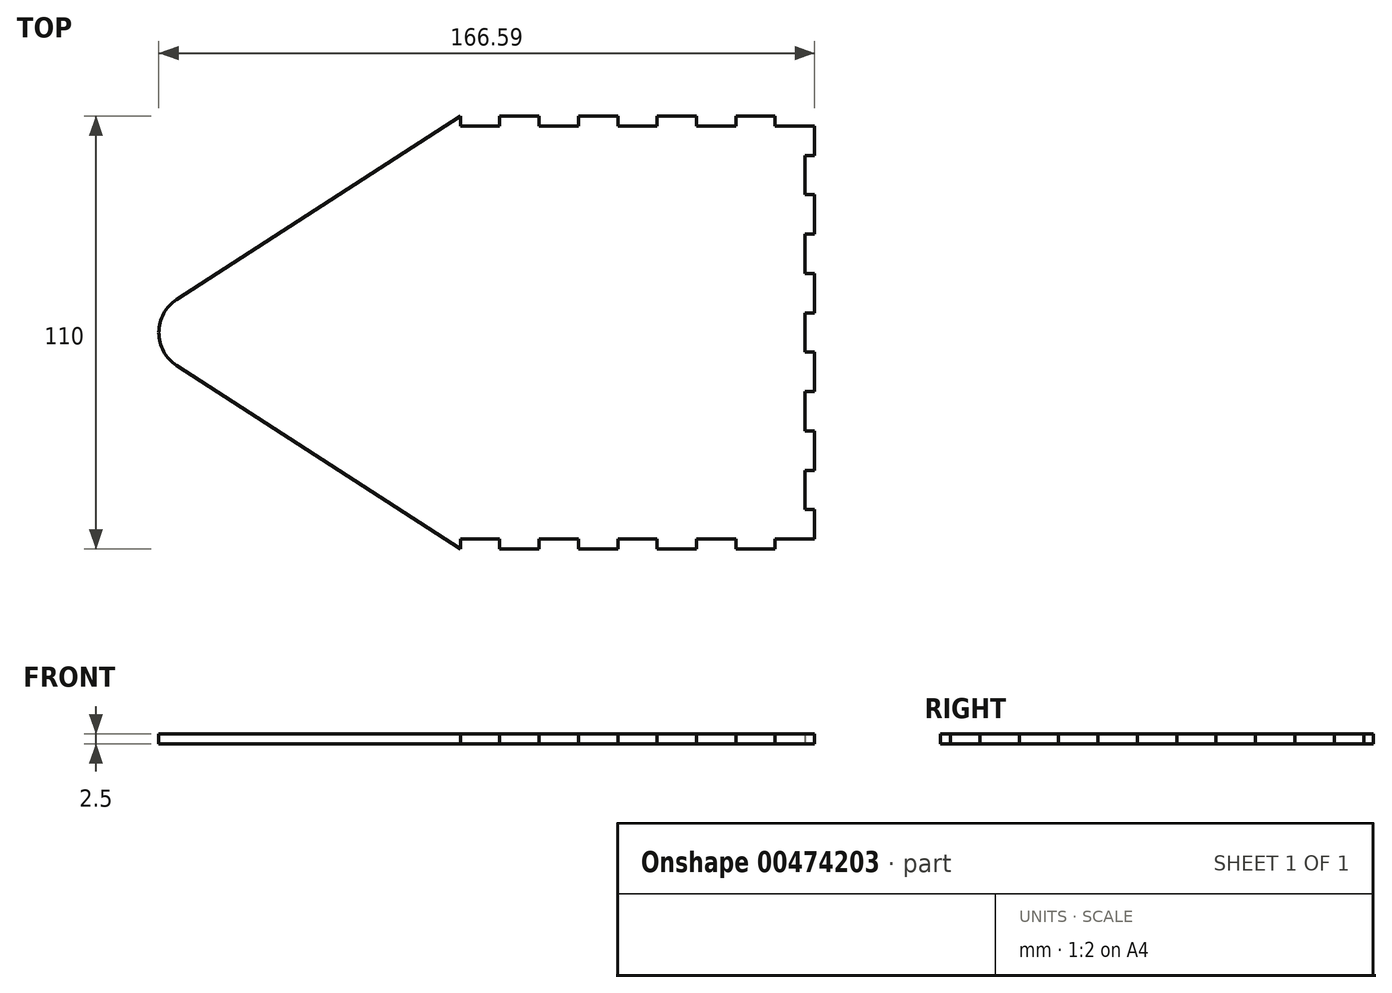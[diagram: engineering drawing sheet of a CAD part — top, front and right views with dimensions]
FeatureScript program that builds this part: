
annotation { "Feature Type Name" : "Feature", "Feature Type Description" : "" }
export const myFeature = defineFeature(function(context is Context, id is Id, definition is map)
    precondition{}
    {
        {
            var Q0;
            Q0=qCreatedBy(makeId("Top.planeOp"),FACE);
            var sketch = newSketch(context, id + "F0", { "sketchPlane" : qUnion([Q0])});
            skLineSegment(sketch, "E0.bottom", {"start": v(75, -55) * mm, "end": v(-15, -55) * mm});
            skLineSegment(sketch, "E0.top", {"start": v(75, 55) * mm, "end": v(-15, 55) * mm});
            skLineSegment(sketch, "E0.left", {"start": v(75, -55) * mm, "end": v(75, 55) * mm});
            skLineSegment(sketch, "E1.bottom", {"start": v(75, 55) * mm, "end": v(65, 55) * mm});
            skLineSegment(sketch, "E1.top", {"start": v(75, 52.5) * mm, "end": v(65, 52.5) * mm});
            skLineSegment(sketch, "E1.left", {"start": v(75, 55) * mm, "end": v(75, 52.5) * mm});
            skLineSegment(sketch, "E1.right", {"start": v(65, 55) * mm, "end": v(65, 52.5) * mm});
            skLineSegment(sketch, "E2.0.1.0", {"start": v(65, -52.5) * mm, "end": v(65, -55) * mm});
            skLineSegment(sketch, "E2.0.1.1", {"start": v(75, -52.5) * mm, "end": v(75, -55) * mm});
            skLineSegment(sketch, "E2.0.1.2", {"start": v(75, -55) * mm, "end": v(65, -55) * mm});
            skLineSegment(sketch, "E2.0.1.3", {"start": v(75, -52.5) * mm, "end": v(65, -52.5) * mm});
            skLineSegment(sketch, "E2.1.0.0", {"start": v(45, 55) * mm, "end": v(45, 52.5) * mm});
            skLineSegment(sketch, "E2.1.0.1", {"start": v(55, 55) * mm, "end": v(55, 52.5) * mm});
            skLineSegment(sketch, "E2.1.0.2", {"start": v(55, 52.5) * mm, "end": v(45, 52.5) * mm});
            skLineSegment(sketch, "E2.1.0.3", {"start": v(55, 55) * mm, "end": v(45, 55) * mm});
            skLineSegment(sketch, "E2.1.1.0", {"start": v(45, -52.5) * mm, "end": v(45, -55) * mm});
            skLineSegment(sketch, "E2.1.1.1", {"start": v(55, -52.5) * mm, "end": v(55, -55) * mm});
            skLineSegment(sketch, "E2.1.1.2", {"start": v(55, -55) * mm, "end": v(45, -55) * mm});
            skLineSegment(sketch, "E2.1.1.3", {"start": v(55, -52.5) * mm, "end": v(45, -52.5) * mm});
            skLineSegment(sketch, "E2.2.0.0", {"start": v(25, 55) * mm, "end": v(25, 52.5) * mm});
            skLineSegment(sketch, "E2.2.0.1", {"start": v(35, 55) * mm, "end": v(35, 52.5) * mm});
            skLineSegment(sketch, "E2.2.0.2", {"start": v(35, 52.5) * mm, "end": v(25, 52.5) * mm});
            skLineSegment(sketch, "E2.2.0.3", {"start": v(35, 55) * mm, "end": v(25, 55) * mm});
            skLineSegment(sketch, "E2.2.1.0", {"start": v(25, -52.5) * mm, "end": v(25, -55) * mm});
            skLineSegment(sketch, "E2.2.1.1", {"start": v(35, -52.5) * mm, "end": v(35, -55) * mm});
            skLineSegment(sketch, "E2.2.1.2", {"start": v(35, -55) * mm, "end": v(25, -55) * mm});
            skLineSegment(sketch, "E2.2.1.3", {"start": v(35, -52.5) * mm, "end": v(25, -52.5) * mm});
            skLineSegment(sketch, "E2.3.0.0", {"start": v(5, 55) * mm, "end": v(5, 52.5) * mm});
            skLineSegment(sketch, "E2.3.0.1", {"start": v(15, 55) * mm, "end": v(15, 52.5) * mm});
            skLineSegment(sketch, "E2.3.0.2", {"start": v(15, 52.5) * mm, "end": v(5, 52.5) * mm});
            skLineSegment(sketch, "E2.3.0.3", {"start": v(15, 55) * mm, "end": v(5, 55) * mm});
            skLineSegment(sketch, "E2.3.1.0", {"start": v(5, -52.5) * mm, "end": v(5, -55) * mm});
            skLineSegment(sketch, "E2.3.1.1", {"start": v(15, -52.5) * mm, "end": v(15, -55) * mm});
            skLineSegment(sketch, "E2.3.1.2", {"start": v(15, -55) * mm, "end": v(5, -55) * mm});
            skLineSegment(sketch, "E2.3.1.3", {"start": v(15, -52.5) * mm, "end": v(5, -52.5) * mm});
            skLineSegment(sketch, "E2.4.0.0", {"start": v(-15, 55) * mm, "end": v(-15, 52.5) * mm});
            skLineSegment(sketch, "E2.4.0.1", {"start": v(-5, 55) * mm, "end": v(-5, 52.5) * mm});
            skLineSegment(sketch, "E2.4.0.2", {"start": v(-5, 52.5) * mm, "end": v(-15, 52.5) * mm});
            skLineSegment(sketch, "E2.4.0.3", {"start": v(-5, 55) * mm, "end": v(-15, 55) * mm});
            skLineSegment(sketch, "E2.4.1.0", {"start": v(-15, -52.5) * mm, "end": v(-15, -55) * mm});
            skLineSegment(sketch, "E2.4.1.1", {"start": v(-5, -52.5) * mm, "end": v(-5, -55) * mm});
            skLineSegment(sketch, "E2.4.1.2", {"start": v(-5, -55) * mm, "end": v(-15, -55) * mm});
            skLineSegment(sketch, "E2.4.1.3", {"start": v(-5, -52.5) * mm, "end": v(-15, -52.5) * mm});
            skLineSegment(sketch, "E2.direction1", {"start": v(65, 52.5) * mm, "end": v(45, 52.5) * mm, "construction": true});
            skLineSegment(sketch, "E2.direction2", {"start": v(65, 52.5) * mm, "end": v(65, 35) * mm, "construction": true});
            skLineSegment(sketch, "E3.1.0.0", {"start": v(75, 45) * mm, "end": v(75, 35) * mm});
            skLineSegment(sketch, "E3.1.0.1", {"start": v(72.5, 45) * mm, "end": v(72.5, 35) * mm});
            skLineSegment(sketch, "E3.1.0.2", {"start": v(72.5, 45) * mm, "end": v(75, 45) * mm});
            skLineSegment(sketch, "E3.1.0.3", {"start": v(72.5, 35) * mm, "end": v(75, 35) * mm});
            skLineSegment(sketch, "E3.1.1.0", {"start": v(75, 25) * mm, "end": v(75, 15) * mm});
            skLineSegment(sketch, "E3.1.1.1", {"start": v(72.5, 25) * mm, "end": v(72.5, 15) * mm});
            skLineSegment(sketch, "E3.1.1.2", {"start": v(72.5, 25) * mm, "end": v(75, 25) * mm});
            skLineSegment(sketch, "E3.1.1.3", {"start": v(72.5, 15) * mm, "end": v(75, 15) * mm});
            skLineSegment(sketch, "E3.1.2.0", {"start": v(75, 5) * mm, "end": v(75, -5) * mm});
            skLineSegment(sketch, "E3.1.2.1", {"start": v(72.5, 5) * mm, "end": v(72.5, -5) * mm});
            skLineSegment(sketch, "E3.1.2.2", {"start": v(72.5, 5) * mm, "end": v(75, 5) * mm});
            skLineSegment(sketch, "E3.1.2.3", {"start": v(72.5, -5) * mm, "end": v(75, -5) * mm});
            skLineSegment(sketch, "E3.1.3.0", {"start": v(75, -15) * mm, "end": v(75, -25) * mm});
            skLineSegment(sketch, "E3.1.3.1", {"start": v(72.5, -15) * mm, "end": v(72.5, -25) * mm});
            skLineSegment(sketch, "E3.1.3.2", {"start": v(72.5, -15) * mm, "end": v(75, -15) * mm});
            skLineSegment(sketch, "E3.1.3.3", {"start": v(72.5, -25) * mm, "end": v(75, -25) * mm});
            skLineSegment(sketch, "E3.1.4.0", {"start": v(75, -35) * mm, "end": v(75, -45) * mm});
            skLineSegment(sketch, "E3.1.4.1", {"start": v(72.5, -35) * mm, "end": v(72.5, -45) * mm});
            skLineSegment(sketch, "E3.1.4.2", {"start": v(72.5, -35) * mm, "end": v(75, -35) * mm});
            skLineSegment(sketch, "E3.1.4.3", {"start": v(72.5, -45) * mm, "end": v(75, -45) * mm});
            skLineSegment(sketch, "E3.direction1", {"start": v(-72.5, 35) * mm, "end": v(75, 35) * mm, "construction": true});
            skLineSegment(sketch, "E4.trimOffspring", {"start": v(65, -52.5) * mm, "end": v(65, -55) * mm, "construction": true});
            skLineSegment(sketch, "E5", {"start": v(0, 0) * mm, "end": v(-100, 0) * mm, "construction": true});
            skLineSegment(sketch, "E6", {"start": v(-15, 55) * mm, "end": v(-100, 0) * mm});
            skLineSegment(sketch, "E7", {"start": v(-15, -55) * mm, "end": v(-100, 0) * mm});
            skSolve(sketch);
        }
        {
            var Q0;
            Q0=makeQuery(id+"F0.imprint","IMPRINT",FACE,{"disambiguationData":[TD([[makeQuery(id+"F0.imprint","IMPRINT",EDGE,{"derivedFrom":sQuery(id+"F0.wireOp",EDGE,"E0.bottom")}),-1.0]])]});
            extrude(context, id + "F1", {"entities" : qUnion([Q0]), "depth" : 2.5 * mm});
        }
        {
            var Q0;
            Q0=makeQuery(id+"F1.opExtrude","SWEPT_EDGE",EDGE,{"disambiguationData":[OSD([sQuery(id+"F0.wireOp",EDGE,"E6"),sQuery(id+"F0.wireOp",EDGE,"E7")])]});
            fillet(context, id + "F2", {"entities" : qUnion([Q0]), "radius" : 10 * mm, "tangentPropagation" : true, "allowEdgeOverflow" : false});
        }
    });
